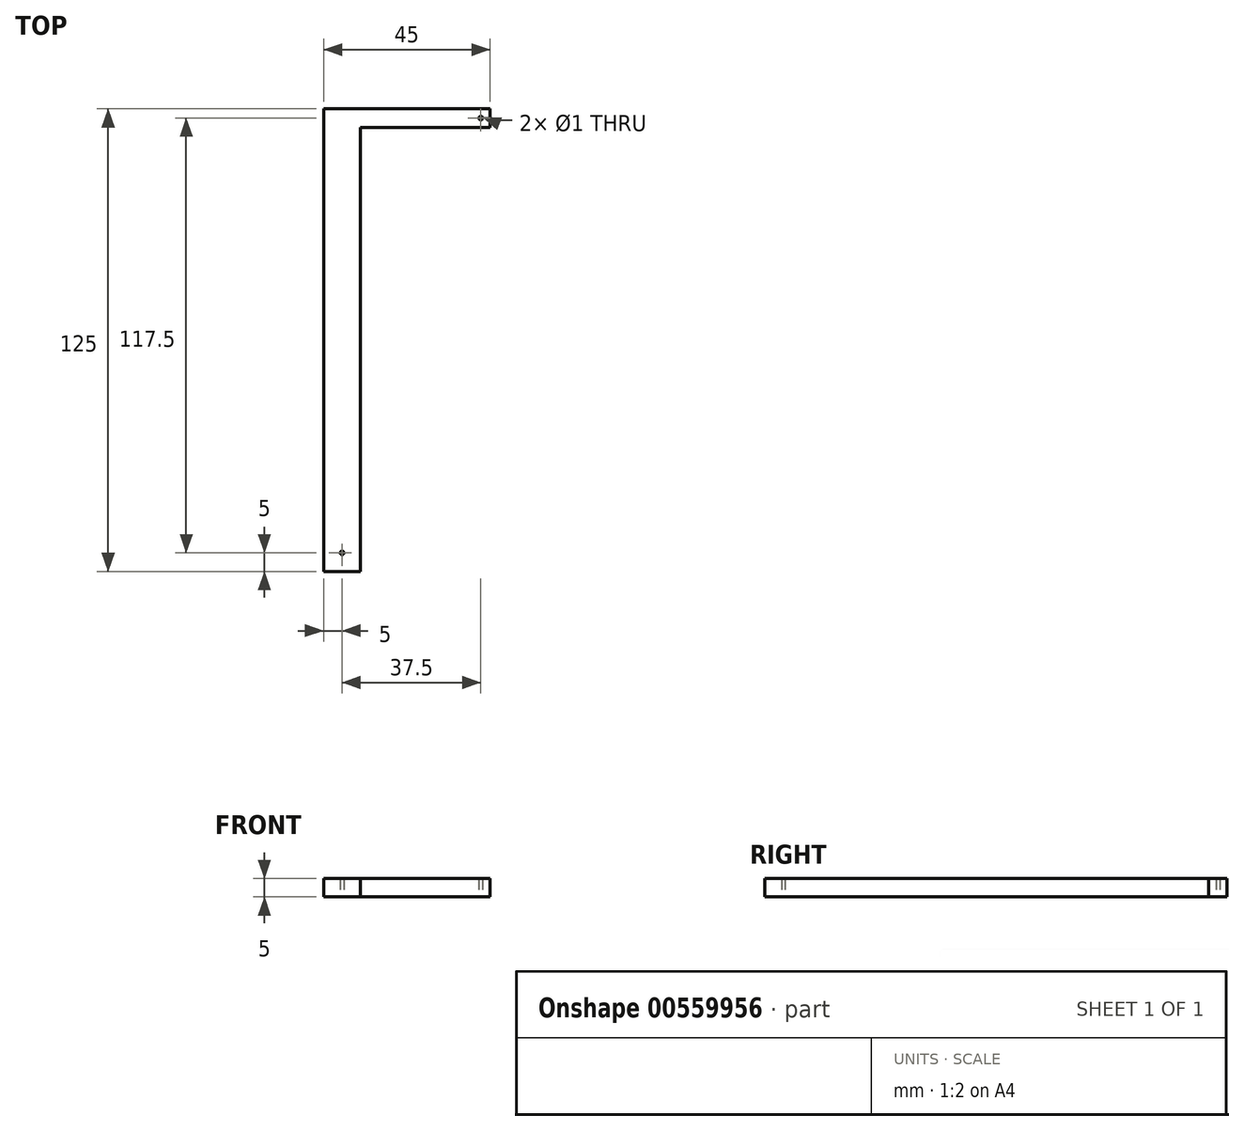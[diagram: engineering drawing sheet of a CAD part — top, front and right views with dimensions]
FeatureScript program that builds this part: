
annotation { "Feature Type Name" : "Feature", "Feature Type Description" : "" }
export const myFeature = defineFeature(function(context is Context, id is Id, definition is map)
    precondition{}
    {
        {
            var Q0;
            Q0=qCreatedBy(makeId("Top.planeOp"),FACE);
            var sketch = newSketch(context, id + "F0", { "sketchPlane" : qUnion([Q0])});
            skLineSegment(sketch, "E0", {"start": v(0, 0) * mm, "end": v(0, 125) * mm});
            skLineSegment(sketch, "E1", {"start": v(0, 125) * mm, "end": v(45, 125) * mm});
            skLineSegment(sketch, "E2", {"start": v(45, 125) * mm, "end": v(45, 120) * mm});
            skLineSegment(sketch, "E3", {"start": v(45, 120) * mm, "end": v(10, 120) * mm});
            skLineSegment(sketch, "E4", {"start": v(10, 120) * mm, "end": v(10, 0) * mm});
            skLineSegment(sketch, "E5", {"start": v(10, 0) * mm, "end": v(0, 0) * mm});
            skCircle(sketch, "E6", {"center": v(5, 5) * mm, "radius": 0.5 * mm});
            skPoint(sketch, "E6.centerSnap0", {"position": v(5, 0) * mm});
            skCircle(sketch, "E7", {"center": v(42.5, 122.5) * mm, "radius": 0.5 * mm});
            skSolve(sketch);
        }
        {
            var Q0;
            Q0=makeQuery(id+"F0.imprint","IMPRINT",FACE,{"disambiguationData":[TD([[makeQuery(id+"F0.imprint","IMPRINT",EDGE,{"derivedFrom":sQuery(id+"F0.wireOp",EDGE,"E0")}),-1.0]])]});
            extrude(context, id + "F1", {"entities" : qUnion([Q0]), "depth" : 5 * mm, "offsetDistance" : 25 * mm});
        }
    });
